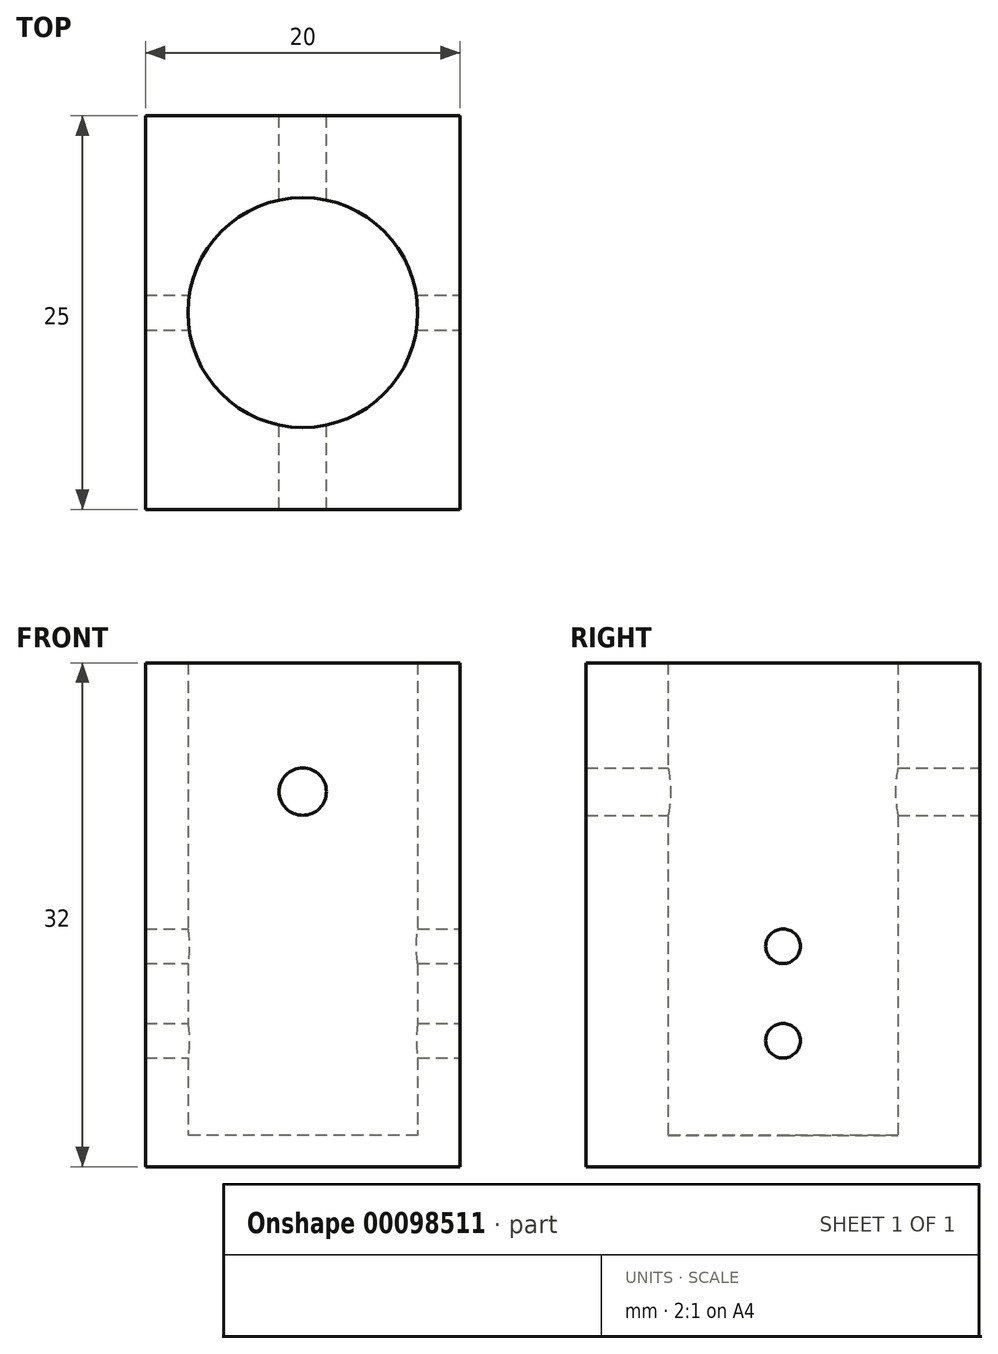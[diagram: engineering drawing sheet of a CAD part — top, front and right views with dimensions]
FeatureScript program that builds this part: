
annotation { "Feature Type Name" : "Feature", "Feature Type Description" : "" }
export const myFeature = defineFeature(function(context is Context, id is Id, definition is map)
    precondition{}
    {
        {
            var Q0;
            Q0=qCreatedBy(makeId("Top.planeOp"),FACE);
            var sketch = newSketch(context, id + "F0", { "sketchPlane" : qUnion([Q0])});
            skLineSegment(sketch, "E0.bottom", {"start": v(10, 12.5) * mm, "end": v(-10, 12.5) * mm});
            skLineSegment(sketch, "E0.top", {"start": v(10, -12.5) * mm, "end": v(-10, -12.5) * mm});
            skLineSegment(sketch, "E0.left", {"start": v(10, 12.5) * mm, "end": v(10, -12.5) * mm});
            skLineSegment(sketch, "E0.right", {"start": v(-10, 12.5) * mm, "end": v(-10, -12.5) * mm});
            skPoint(sketch, "E0.middle", {"position": v(0, 0) * mm});
            skCircle(sketch, "E1", {"center": v(0, 0) * mm, "radius": 7.3 * mm});
            skSolve(sketch);
        }
        {
            var Q0;
            Q0=makeQuery(id+"F0.imprint","IMPRINT",FACE,{"disambiguationData":[TD([[makeQuery(id+"F0.imprint","IMPRINT",EDGE,{"derivedFrom":sQuery(id+"F0.wireOp",EDGE,"E0.bottom")}),1.0]])]});
            extrude(context, id + "F1", {"entities" : qUnion([Q0]), "depth" : 30 * mm});
        }
        {
            var Q0;
            Q0=makeQuery(id+"F1.opExtrude","SWEPT_FACE",FACE,{"disambiguationData":[OSD([sQuery(id+"F0.wireOp",EDGE,"E0.left")])]});
            var sketch = newSketch(context, id + "F2", { "sketchPlane" : qUnion([Q0])});
            skLineSegment(sketch, "E2", {"start": v(0, 0) * mm, "end": v(0, 6) * mm});
            skPoint(sketch, "E2.endSnap0", {"position": v(0, 0) * mm});
            skCircle(sketch, "E3", {"center": v(0, 6) * mm, "radius": 1.1 * mm});
            skLineSegment(sketch, "E4", {"start": v(0, 6) * mm, "end": v(0, 12) * mm});
            skCircle(sketch, "E5", {"center": v(0, 12) * mm, "radius": 1.1 * mm});
            skSolve(sketch);
        }
        {
            var Q0;
            Q0 = qSketchRegion(id + "F2", true);
            extrude(context, id + "F3", {"entities" : qUnion([Q0]), "operationType" : NewBodyOperationType.REMOVE, "oppositeDirection" : true, "depth" : 25 * mm});
        }
        {
            var Q0;
            Q0=makeQuery(id+"F1.opExtrude","SWEPT_FACE",FACE,{"disambiguationData":[OSD([sQuery(id+"F0.wireOp",EDGE,"E0.bottom")])]});
            var sketch = newSketch(context, id + "F4", { "sketchPlane" : qUnion([Q0])});
            skLineSegment(sketch, "E6", {"start": v(0, 0) * mm, "end": v(0, 21.82) * mm});
            skCircle(sketch, "E7", {"center": v(0, 21.82) * mm, "radius": 1.5 * mm});
            skSolve(sketch);
        }
        {
            var Q0;
            Q0 = qSketchRegion(id + "F4", true);
            extrude(context, id + "F5", {"entities" : qUnion([Q0]), "operationType" : NewBodyOperationType.REMOVE, "endBound" : BoundingType.THROUGH_ALL, "oppositeDirection" : true, "depth" : 25 * mm});
        }
        {
            var Q0;
            Q0=makeQuery(id+"F1.opExtrude","CAP_FACE",FACE,{"disambiguationData":[OSD([sQuery(id+"F0.wireOp",EDGE,"E0.bottom"),sQuery(id+"F0.wireOp",EDGE,"E0.top"),sQuery(id+"F0.wireOp",EDGE,"E0.left"),sQuery(id+"F0.wireOp",EDGE,"E0.right"),sQuery(id+"F0.wireOp",EDGE,"E1")])],"isStart":true});
            var sketch = newSketch(context, id + "F6", { "sketchPlane" : qUnion([Q0])});
            skLineSegment(sketch, "E8.bottom", {"start": v(-10, -12.5) * mm, "end": v(10, -12.5) * mm});
            skLineSegment(sketch, "E8.top", {"start": v(-10, 12.5) * mm, "end": v(10, 12.5) * mm});
            skLineSegment(sketch, "E8.left", {"start": v(-10, -12.5) * mm, "end": v(-10, 12.5) * mm});
            skLineSegment(sketch, "E8.right", {"start": v(10, -12.5) * mm, "end": v(10, 12.5) * mm});
            skSolve(sketch);
        }
        {
            var Q0;
            Q0 = qSketchRegion(id + "F6", true);
            extrude(context, id + "F7", {"entities" : qUnion([Q0]), "operationType" : NewBodyOperationType.ADD, "depth" : 2 * mm});
        }
    });
